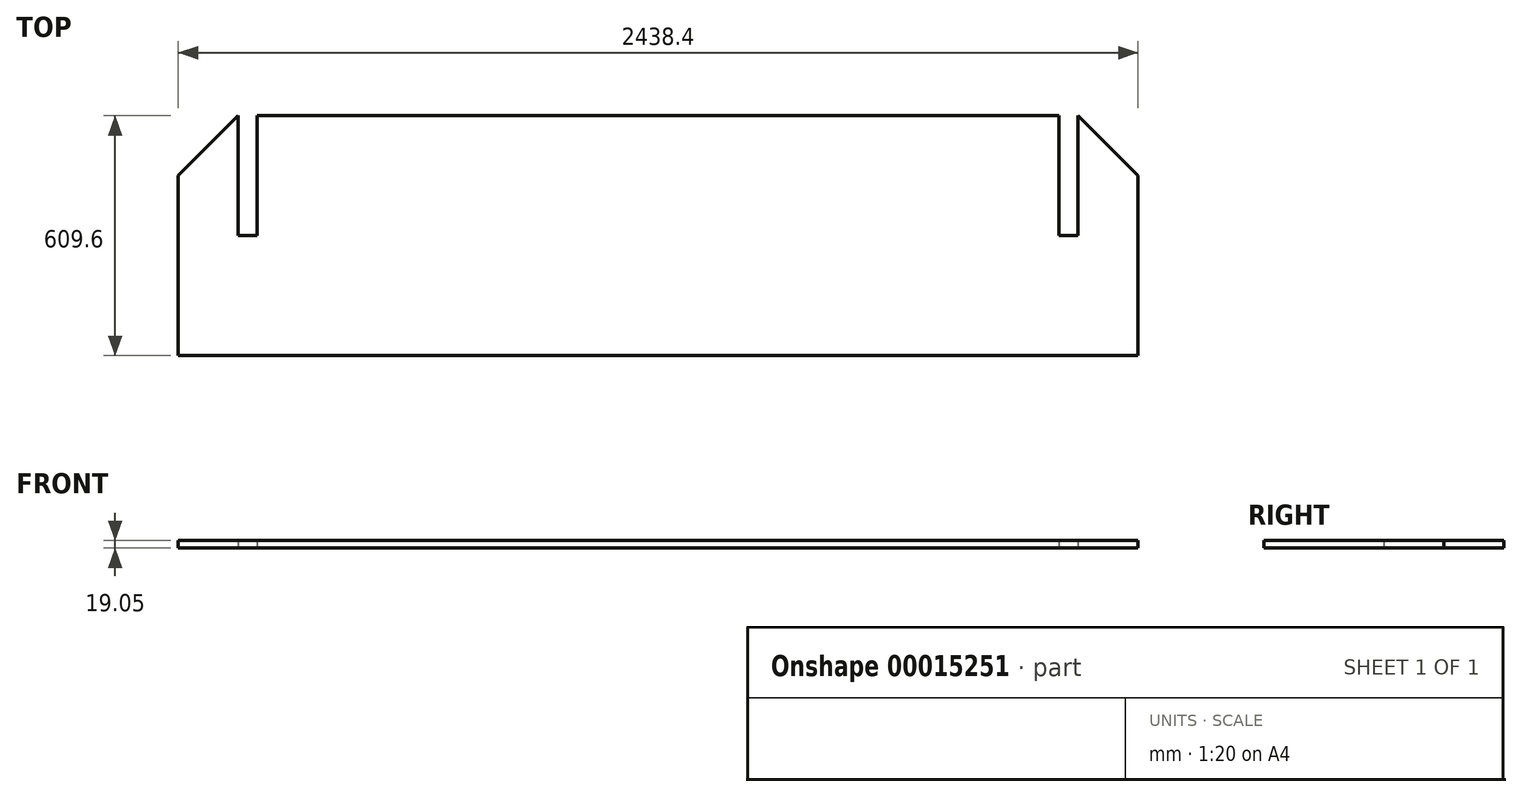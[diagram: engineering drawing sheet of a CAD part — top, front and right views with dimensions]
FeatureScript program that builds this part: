
annotation { "Feature Type Name" : "Feature", "Feature Type Description" : "" }
export const myFeature = defineFeature(function(context is Context, id is Id, definition is map)
    precondition{}
    {
        {
            var Q0;
            Q0=qCreatedBy(makeId("Top.planeOp"),FACE);
            var sketch = newSketch(context, id + "F0", { "sketchPlane" : qUnion([Q0])});
            skLineSegment(sketch, "E0.bottom", {"start": v(-1035.17, 347.63) * mm, "end": v(1001.91, 347.63) * mm});
            skLineSegment(sketch, "E0.top", {"start": v(-1235.83, -261.97) * mm, "end": v(1202.57, -261.97) * mm});
            skLineSegment(sketch, "E0.left", {"start": v(-1235.83, 347.63) * mm, "end": v(-1235.83, -261.97) * mm});
            skLineSegment(sketch, "E0.right", {"start": v(1202.57, 347.63) * mm, "end": v(1202.57, -261.97) * mm});
            skLineSegment(sketch, "E1", {"start": v(-1083.43, 347.63) * mm, "end": v(-1235.83, 195.23) * mm});
            skLineSegment(sketch, "E2", {"start": v(1050.17, 347.63) * mm, "end": v(1202.57, 195.23) * mm});
            skLineSegment(sketch, "E3.top", {"start": v(-1083.43, 42.83) * mm, "end": v(-1035.17, 42.83) * mm});
            skLineSegment(sketch, "E3.left", {"start": v(-1083.43, 347.63) * mm, "end": v(-1083.43, 42.83) * mm});
            skLineSegment(sketch, "E3.right", {"start": v(-1035.17, 347.63) * mm, "end": v(-1035.17, 42.83) * mm});
            skLineSegment(sketch, "E4.top", {"start": v(1050.17, 42.83) * mm, "end": v(1001.91, 42.83) * mm});
            skLineSegment(sketch, "E4.left", {"start": v(1050.17, 347.63) * mm, "end": v(1050.17, 42.83) * mm});
            skLineSegment(sketch, "E4.right", {"start": v(1001.91, 347.63) * mm, "end": v(1001.91, 42.83) * mm});
            skSolve(sketch);
        }
        {
            var Q0;
            Q0=qSketchRegion(id+"F0",true);
            extrude(context, id + "F1", {"entities" : qUnion([Q0]), "depth" : 19.05 * mm});
        }
    });
